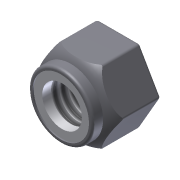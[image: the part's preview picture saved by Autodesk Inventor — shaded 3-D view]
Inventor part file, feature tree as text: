
AUTODESK INVENTOR PART (.ipt)
format: ipt  version: 2011 (Build 150239000, 239)  size: 188,416 bytes
history: native  units: in
note: dims shown in document units (in); Inventor stores cm internally (conversion verified against a paired STEP export)
features: sketch x5, extrude x3, fillet x2, hole x1, revolve x1, projected_geometry x1
ambient origin geometry x8: Origin, YZ Plane, XZ Plane, XY Plane, X Axis, Y Axis, Z Axis, Center Point
bodies: Solid1 (feature_tree)
feature tree (13):
  extrude  "Extrusion1"  Depth=0.375in TaperAngle=0.0deg
  extrude  "Extrusion2"  Depth=0.0781in TaperAngle=0.0deg
  extrude  "Extrusion3"  Depth=0.01in TaperAngle=0.0deg
  hole  "Hole2"  [1 undecoded]
  revolve  "Revolution2"  [1 undecoded]
  fillet  "Fillet1"  Radius=0.02in
  fillet  "Fillet2"  Radius=0.4062in
  sketch  "Sketch1"  dims[d0=0.5625in d1=0.375in d2=0.0in]
  sketch  "Sketch3"  dims[d3=0.5in d4=0.0781in d5=0.0in]
  sketch  "Sketch8"  dims[d14=0.4375in d15=0.01in d16=0.0in]
  sketch  "Sketch9"  dims[d17=0.307in d18=0.375in d19=0.375in d20=0.25in d21=0.5635in d22=1.0in d23=0.8108in d24=0.18in]
  sketch  "Sketch10"  dims[d25=90.0deg d26=0.02in d27=0.02in d28=0.4062in]
  projected_geometry  "Projected Loop8"
note: 2 required parameter values undecoded (feature->parameter linkage not recoverable at this tier; creation-order binding heuristic only, values carry confidence <= 0.55)